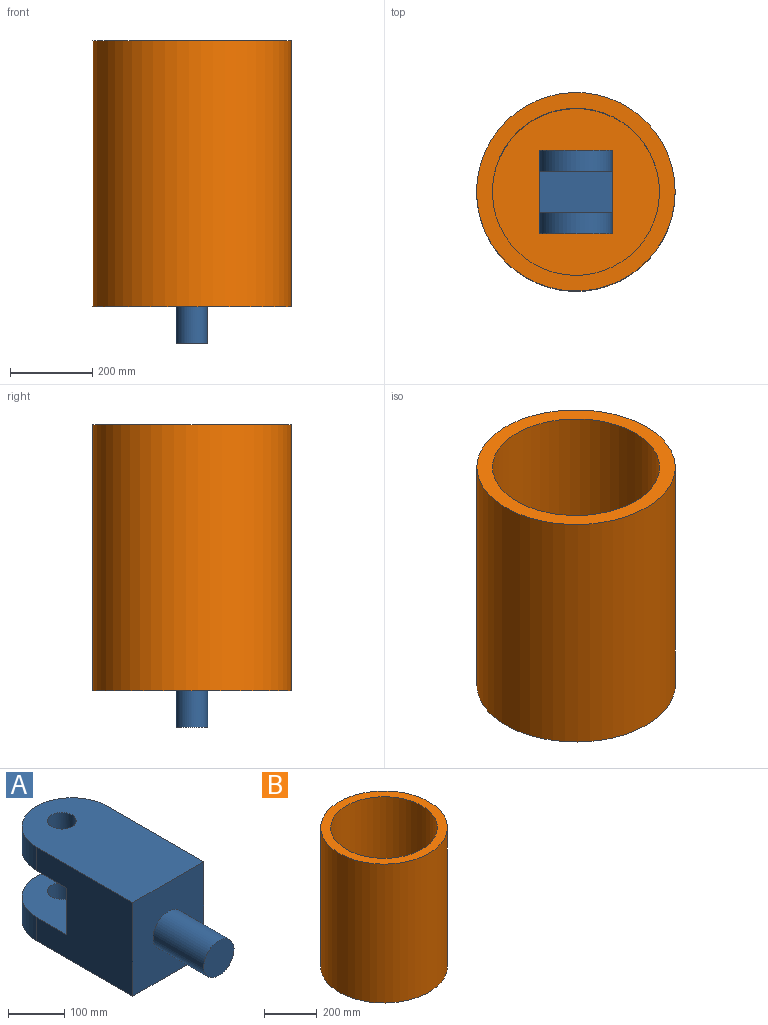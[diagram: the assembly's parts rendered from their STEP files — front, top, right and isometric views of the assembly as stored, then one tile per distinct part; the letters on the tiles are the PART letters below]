
ASSEMBLY  parts=2 mates=1
PART A: 14 faces, bbox 177.8x457.2x203.2 mm
  f0: plane 241.3x203.2mm, normal (1,0,0), area 41290.2mm2, adj f2,f5,f6,f7,f8,f9,f10,f11
  f1: cylinder r=25.4mm len=50.8mm, axis (0,0,-1), area 8107.3mm2, adj f5,f9
  f2: plane 203.2x177.8mm, normal (0,-1,0), area 31568.6mm2, adj f0,f4,f5,f6,f12
  f3: cylinder r=25.4mm len=50.8mm, axis (0,0,-1), area 8107.3mm2, adj f6,f8
  f4: plane 241.3x203.2mm, normal (-1,0,0), area 41290.2mm2, adj f2,f5,f6,f7,f8,f9,f10,f11
  f5: plane 330.2x177.8mm, normal (0,0,1), area 53290.6mm2, adj f0,f1,f2,f4,f11
  f6: plane 330.2x177.8mm, normal (0,0,-1), area 53290.6mm2, adj f0,f2,f3,f4,f10
  f7: plane 177.8x101.6mm, normal (0,1,0), area 18064.5mm2, adj f0,f4,f8,f9
  f8: plane 177.8x165.1mm, normal (0,0,1), area 23935.9mm2, adj f0,f3,f4,f7,f10
  f9: plane 177.8x165.1mm, normal (0,0,-1), area 23935.9mm2, adj f0,f1,f4,f7,f11
  f10: cylinder r=88.9mm len=177.8mm, axis (0,0,1), area 14187.8mm2, adj f0,f4,f6,f8
  f11: cylinder r=88.9mm len=177.8mm, axis (0,0,1), area 14187.8mm2, adj f0,f4,f5,f9
  f12: cylinder r=38.1mm len=127mm, axis (0,1,0), area 30402.4mm2, adj f2,f13
  f13: plane 76.2x76.2mm, normal (0,-1,0), area 4560.4mm2, adj f12
PART B: 6 faces, bbox 482.6x482.6x647.7 mm
  f0: cylinder r=38.1mm len=76.2mm, axis (0,0,-1), area 9120.7mm2, adj f3,f5
  f1: cylinder r=241.3mm len=647.7mm, axis (0,0,-1), area 981999.1mm2, adj f2,f3
  f2: plane 482.6x482.6mm, normal (0,0,1), area 53204.3mm2, adj f1,f4
  f3: plane 482.6x482.6mm, normal (0,0,-1), area 178361mm2, adj f0,f1
  f4: cylinder r=203.2mm len=609.6mm, axis (0,0,-1), area 778302.7mm2, adj f2,f5
  f5: plane 406.4x406.4mm, normal (0,0,1), area 125156.7mm2, adj f0,f4
PLACE A rot(axis=(1,0,0),90deg) t=(-12781.17,1879.44,-4949.02)mm
PLACE B t=(-15752.97,-3124.36,-402.42)mm
MATE fastened A.f12 <-> B.f0  axis (0,0,-1) through (3170.03,1777.84,-364.32)mm
